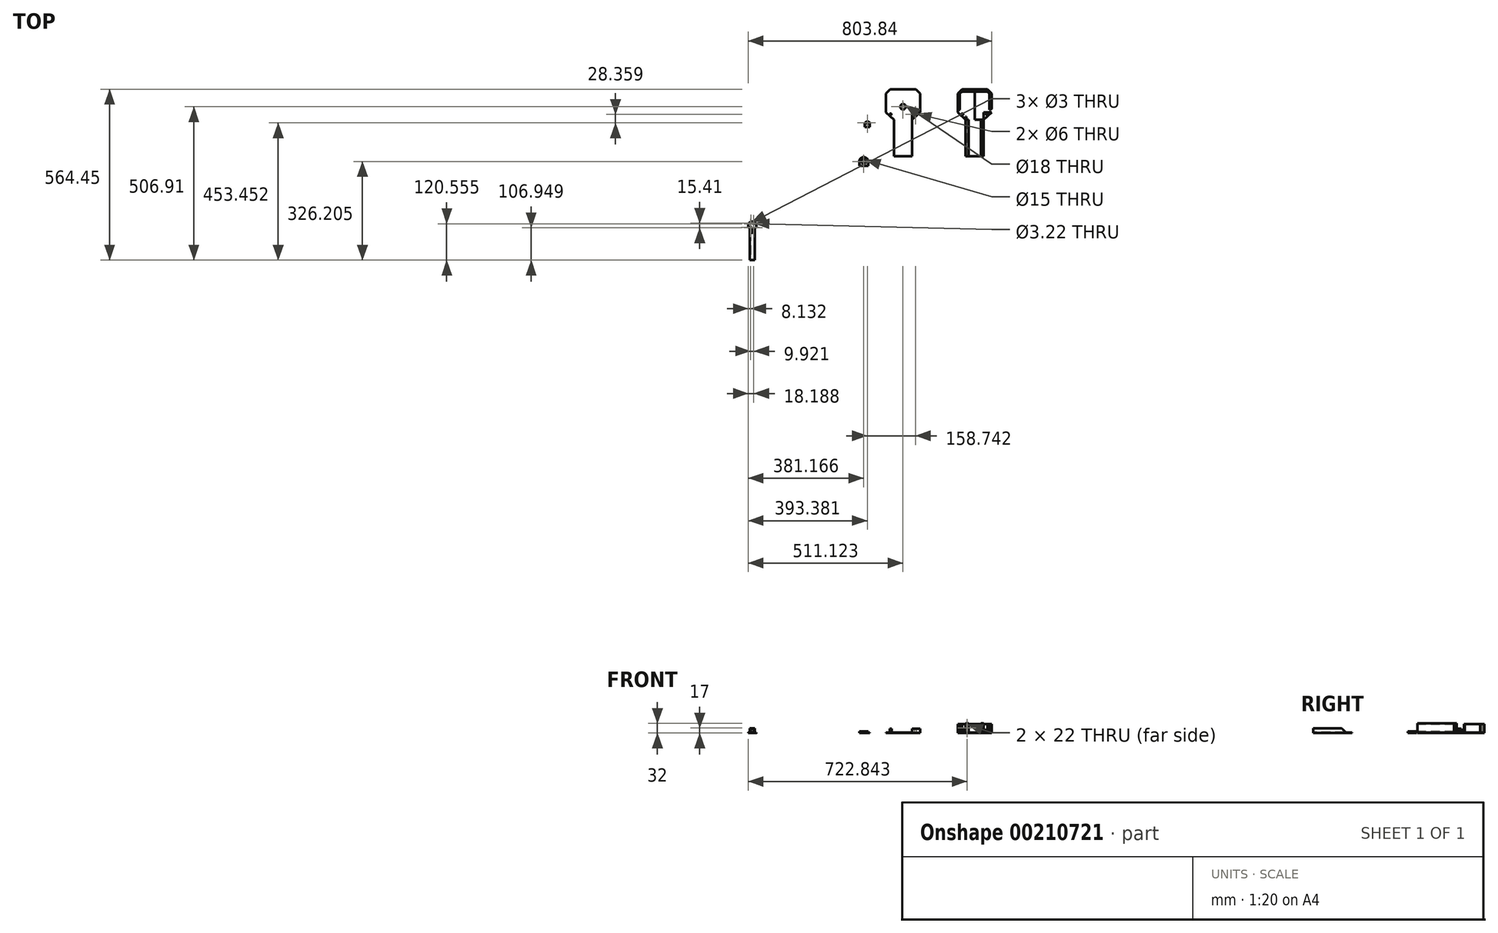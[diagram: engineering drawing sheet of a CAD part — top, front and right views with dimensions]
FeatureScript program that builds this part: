
annotation { "Feature Type Name" : "Feature", "Feature Type Description" : "" }
export const myFeature = defineFeature(function(context is Context, id is Id, definition is map)
    precondition{}
    {
        {
            var Q0;
            Q0=qCreatedBy(makeId("Top.planeOp"),FACE);
            var sketch = newSketch(context, id + "F0", { "sketchPlane" : qUnion([Q0])});
            skLineSegment(sketch, "E0.bottom", {"start": v(135.29, -55.36) * mm, "end": v(160.29, -55.36) * mm});
            skLineSegment(sketch, "E0.top", {"start": v(135.29, -70.36) * mm, "end": v(160.29, -70.36) * mm});
            skLineSegment(sketch, "E0.left", {"start": v(135.29, -55.36) * mm, "end": v(135.29, -70.36) * mm});
            skLineSegment(sketch, "E0.right", {"start": v(160.29, -55.36) * mm, "end": v(160.29, -70.36) * mm});
            skArc(sketch, "E1", {"start": v(160.29, -55.36) * mm, "mid": v(147.79, -42.86) * mm, "end": v(135.29, -55.36) * mm});
            skPoint(sketch, "E2", {"position": v(147.79, -62.86) * mm});
            skLineSegment(sketch, "E3.bottom", {"start": v(133.29, -55.36) * mm, "end": v(162.29, -55.36) * mm});
            skLineSegment(sketch, "E3.top", {"start": v(133.29, -70.36) * mm, "end": v(162.29, -70.36) * mm});
            skLineSegment(sketch, "E3.left", {"start": v(133.29, -55.36) * mm, "end": v(133.29, -70.36) * mm});
            skLineSegment(sketch, "E3.right", {"start": v(162.29, -55.36) * mm, "end": v(162.29, -70.36) * mm});
            skArc(sketch, "E4", {"start": v(162.29, -55.36) * mm, "mid": v(147.79, -40.86) * mm, "end": v(133.29, -55.36) * mm});
            skLineSegment(sketch, "E5", {"start": v(135.29, -68.36) * mm, "end": v(160.29, -68.36) * mm});
            skPoint(sketch, "E6", {"position": v(162.29, -63.36) * mm});
            skPoint(sketch, "E7", {"position": v(133.29, -63.36) * mm});
            skCircle(sketch, "E8", {"center": v(-219.9, -267.1) * mm, "radius": 13.48 * mm});
            skPoint(sketch, "E9", {"position": v(-225.25, -272.96) * mm});
            skPoint(sketch, "E10", {"position": v(-225.04, -259.21) * mm});
            skPoint(sketch, "E11", {"position": v(-215.33, -274.62) * mm});
            skPoint(sketch, "E12", {"position": v(-215.2, -261.01) * mm});
            skCircle(sketch, "E13", {"center": v(-225.04, -259.21) * mm, "radius": 1.5 * mm});
            skCircle(sketch, "E14", {"center": v(-215.2, -261.01) * mm, "radius": 1.61 * mm});
            skCircle(sketch, "E15", {"center": v(-215.33, -274.62) * mm, "radius": 1.5 * mm});
            skCircle(sketch, "E16", {"center": v(-225.25, -272.96) * mm, "radius": 1.5 * mm});
            skLineSegment(sketch, "E17", {"start": v(-215.33, -274.62) * mm, "end": v(-215.33, -273.12) * mm});
            skLineSegment(sketch, "E18", {"start": v(-215.33, -259.4) * mm, "end": v(-215.33, -262.62) * mm});
            skLineSegment(sketch, "E19", {"start": v(-225.04, -259.21) * mm, "end": v(-225.06, -260.71) * mm});
            skLineSegment(sketch, "E20", {"start": v(-225.25, -272.96) * mm, "end": v(-225.25, -274.46) * mm});
            skLineSegment(sketch, "E21", {"start": v(-225.25, -279.48) * mm, "end": v(-225.23, -277.57) * mm});
            skLineSegment(sketch, "E22", {"start": v(-225.04, -259.21) * mm, "end": v(-225.04, -254.64) * mm});
            skLineSegment(sketch, "E23.bottom", {"start": v(-225.25, -277.57) * mm, "end": v(-225.23, -277.57) * mm});
            skLineSegment(sketch, "E23.top", {"start": v(-228.4, -381.57) * mm, "end": v(-211.4, -381.57) * mm});
            skLineSegment(sketch, "E23.left", {"start": v(-228.4, -277.57) * mm, "end": v(-228.4, -381.57) * mm});
            skLineSegment(sketch, "E23.right", {"start": v(-211.4, -277.57) * mm, "end": v(-211.4, -381.57) * mm});
            skLineSegment(sketch, "E24.trimOffspring", {"start": v(-215.33, -273.12) * mm, "end": v(-215.33, -276.12) * mm});
            skPoint(sketch, "E25.orphan", {"position": v(-215.33, -279.78) * mm});
            skLineSegment(sketch, "E26.trimOffspring", {"start": v(-215.33, -262.62) * mm, "end": v(-215.33, -254.42) * mm});
            skLineSegment(sketch, "E27.trimOffspring", {"start": v(-225.23, -271.46) * mm, "end": v(-225.25, -272.96) * mm});
            skLineSegment(sketch, "E28.trimOffspring", {"start": v(-225.2, -274.45) * mm, "end": v(-225.16, -271.46) * mm});
            skLineSegment(sketch, "E29.trimOffspring", {"start": v(-225.05, -260.71) * mm, "end": v(-225.04, -259.21) * mm});
            skSolve(sketch);
        }
        {
            var Q0;
            {var subQ0=sQuery(id+"F0.wireOp",EDGE,"E1");Q0=makeQuery(id+"F0.imprint","IMPRINT",FACE,{"disambiguationData":[TD([[makeQuery(id+"F0.imprint","IMPRINT",EDGE,{"derivedFrom":subQ0}),-1.0]])]});}
            var Q1;
            {var subQ3=sQuery(id+"F0.wireOp",EDGE,"E3.right");Q1=makeQuery(id+"F0.imprint","IMPRINT",FACE,{"disambiguationData":[TD([[makeQuery(id+"F0.imprint","IMPRINT",EDGE,{"derivedFrom":subQ3}),-1.0]])]});}
            var Q2;
            {var subQ3=sQuery(id+"F0.wireOp",EDGE,"E5");Q2=makeQuery(id+"F0.imprint","IMPRINT",FACE,{"disambiguationData":[TD([[makeQuery(id+"F0.imprint","IMPRINT",EDGE,{"derivedFrom":subQ3}),-1.0]])]});}
            var Q3;
            {var subQ3=sQuery(id+"F0.wireOp",EDGE,"E3.left");Q3=makeQuery(id+"F0.imprint","IMPRINT",FACE,{"disambiguationData":[TD([[makeQuery(id+"F0.imprint","IMPRINT",EDGE,{"derivedFrom":subQ3}),1.0]])]});}
            var Q4;
            {var subQ4=sQuery(id+"F0.wireOp",EDGE,"E5");Q4=makeQuery(id+"F0.imprint","IMPRINT",FACE,{"disambiguationData":[TD([[makeQuery(id+"F0.imprint","IMPRINT",EDGE,{"derivedFrom":subQ4}),1.0]])]});}
            var Q5;
            {var subQ0=sQuery(id+"F0.wireOp",EDGE,"E1");Q5=makeQuery(id+"F0.imprint","IMPRINT",FACE,{"disambiguationData":[TD([[makeQuery(id+"F0.imprint","IMPRINT",EDGE,{"derivedFrom":subQ0}),1.0]])]});}
            extrude(context, id + "F1", {"entities" : qUnion([Q0, Q1, Q2, Q3, Q4, Q5]), "depth" : 5 * mm});
        }
        {
            var Q0;
            Q0=sQuery(id+"F0.wireOp",VERTEX,"E4.center");
            var Q1;
            Q1=makeQuery(id+"F1.opExtrude","SWEPT_BODY",BODY,{"disambiguationData":[OSD([sQuery(id+"F0.wireOp",EDGE,"E3.top"),sQuery(id+"F0.wireOp",EDGE,"E3.left"),sQuery(id+"F0.wireOp",EDGE,"E3.right"),sQuery(id+"F0.wireOp",EDGE,"E4")])]});
            hole(context, id + "F2", {"style" : HoleStyle.SIMPLE, "endStyle" : HoleEndStyle.BLIND, "oppositeDirection" : true, "holeDiameter" : 15 * mm, "holeDepth" : 12 * mm, "tappedDepth" : 12 * mm, "tapClearance" : 3, "locations" : qUnion([Q0]), "scope" : qUnion([Q1])});
        }
        {
            var Q0;
            Q0=qCreatedBy(makeId("Top.planeOp"),FACE);
            var sketch = newSketch(context, id + "F3", { "sketchPlane" : qUnion([Q0])});
            skLineSegment(sketch, "E30.bottom", {"start": v(247.74, 82.27) * mm, "end": v(307.74, 82.27) * mm});
            skLineSegment(sketch, "E30.top", {"start": v(247.74, -37.73) * mm, "end": v(307.74, -37.73) * mm});
            skLineSegment(sketch, "E30.left", {"start": v(247.74, 82.27) * mm, "end": v(247.74, -37.73) * mm});
            skLineSegment(sketch, "E30.right", {"start": v(307.74, 82.27) * mm, "end": v(307.74, -37.73) * mm});
            skPoint(sketch, "E31.MirrorCS.start.orphan", {"position": v(308.47, -37.03) * mm});
            skPoint(sketch, "E32.end.orphan", {"position": v(277.74, -37.73) * mm});
            skPoint(sketch, "E32.start.orphan", {"position": v(277.74, 82.27) * mm});
            skLineSegment(sketch, "E33", {"start": v(257.74, 82.27) * mm, "end": v(257.74, -37.73) * mm});
            skLineSegment(sketch, "E34", {"start": v(297.74, -37.73) * mm, "end": v(297.74, 82.27) * mm});
            skLineSegment(sketch, "E35.bottom", {"start": v(-60.02, 19.85) * mm, "end": v(-48.02, 19.85) * mm});
            skLineSegment(sketch, "E35.top", {"start": v(-60.02, 7.85) * mm, "end": v(-48.02, 7.85) * mm});
            skLineSegment(sketch, "E35.left", {"start": v(-60.02, 19.85) * mm, "end": v(-60.02, 7.85) * mm});
            skLineSegment(sketch, "E35.right", {"start": v(-48.02, 19.85) * mm, "end": v(-48.02, 7.85) * mm});
            skLineSegment(sketch, "E36", {"start": v(277.74, 182.88) * mm, "end": v(319.8, 182.88) * mm});
            skLineSegment(sketch, "E37", {"start": v(277.74, 182.88) * mm, "end": v(235.68, 182.88) * mm});
            skLineSegment(sketch, "E38", {"start": v(221.74, 168.95) * mm, "end": v(221.74, 107.24) * mm});
            skLineSegment(sketch, "E39", {"start": v(333.74, 168.95) * mm, "end": v(333.74, 107.24) * mm});
            skLineSegment(sketch, "E40", {"start": v(307.74, 82.27) * mm, "end": v(333.74, 107.24) * mm});
            skLineSegment(sketch, "E41.MirrorCS", {"start": v(247.74, 82.2) * mm, "end": v(221.74, 107.24) * mm});
            skLineSegment(sketch, "E42", {"start": v(277.74, 182.88) * mm, "end": v(277.74, -37.73) * mm});
            skLineSegment(sketch, "E43", {"start": v(247.74, 82.27) * mm, "end": v(247.74, 107.24) * mm});
            skLineSegment(sketch, "E44", {"start": v(247.74, 107.24) * mm, "end": v(221.74, 107.24) * mm});
            skCircle(sketch, "E45", {"center": v(236.74, 100.24) * mm, "radius": 3 * mm});
            skLineSegment(sketch, "E46", {"start": v(236.74, 103.24) * mm, "end": v(236.74, 97.24) * mm});
            skLineSegment(sketch, "E47.bottom", {"start": v(151.5, 68.38) * mm, "end": v(168.5, 68.38) * mm});
            skLineSegment(sketch, "E47.top", {"start": v(151.5, 58.38) * mm, "end": v(168.5, 58.38) * mm});
            skLineSegment(sketch, "E47.left", {"start": v(151.5, 68.38) * mm, "end": v(151.5, 58.38) * mm});
            skLineSegment(sketch, "E47.right", {"start": v(168.5, 68.38) * mm, "end": v(168.5, 58.38) * mm});
            skLineSegment(sketch, "E48", {"start": v(160, 68.38) * mm, "end": v(160, 76.88) * mm});
            skPoint(sketch, "E49", {"position": v(160, 74.88) * mm});
            skPoint(sketch, "E50", {"position": v(160, 68.88) * mm});
            skLineSegment(sketch, "E51", {"start": v(160, 74.88) * mm, "end": v(160, 68.88) * mm});
            skCircle(sketch, "E52", {"center": v(160, 71.88) * mm, "radius": 3 * mm});
            skArc(sketch, "E53", {"start": v(168.5, 68.38) * mm, "mid": v(160, 76.88) * mm, "end": v(151.5, 68.38) * mm});
            skCircle(sketch, "E54.MirrorC", {"center": v(318.74, 100.24) * mm, "radius": 3 * mm});
            skLineSegment(sketch, "E55.MirrorCS", {"start": v(307.74, 82.27) * mm, "end": v(307.74, 107.24) * mm});
            skLineSegment(sketch, "E56.MirrorCS", {"start": v(307.74, 107.24) * mm, "end": v(333.74, 107.24) * mm});
            skLineSegment(sketch, "E57", {"start": v(221.74, 168.95) * mm, "end": v(235.68, 182.88) * mm});
            skLineSegment(sketch, "E58.MirrorCS", {"start": v(333.74, 168.95) * mm, "end": v(319.8, 182.88) * mm});
            skPoint(sketch, "E59.endSnap0", {"position": v(228.7, 175.92) * mm});
            skLineSegment(sketch, "E60.MirrorCS", {"start": v(556.53, 182.88) * mm, "end": v(556.53, 175.92) * mm});
            skLineSegment(sketch, "E61.MirrorCS", {"start": v(570.46, 168.95) * mm, "end": v(556.53, 182.88) * mm});
            skLineSegment(sketch, "E62.MirrorCS", {"start": v(555.46, 103.24) * mm, "end": v(555.46, 97.24) * mm});
            skArc(sketch, "E63.MirrorCS", {"start": v(563.5, 118.67) * mm, "mid": v(563.39, 117.04) * mm, "end": v(563.06, 115.43) * mm});
            skLineSegment(sketch, "E64.MirrorCS", {"start": v(556.53, 175.92) * mm, "end": v(563.5, 168.95) * mm});
            skCircle(sketch, "E65.MirrorC", {"center": v(555.46, 100.24) * mm, "radius": 3 * mm});
            skCircle(sketch, "E66.MirrorC", {"center": v(473.46, 100.24) * mm, "radius": 3 * mm});
            skLineSegment(sketch, "E67.MirrorCS", {"start": v(458.46, 168.95) * mm, "end": v(472.4, 182.88) * mm});
            skLineSegment(sketch, "E68.MirrorCS", {"start": v(544.46, 82.27) * mm, "end": v(544.46, 107.24) * mm});
            skLineSegment(sketch, "E69.MirrorCS", {"start": v(556.53, 175.92) * mm, "end": v(514.46, 175.92) * mm});
            skLineSegment(sketch, "E70.MirrorCS", {"start": v(484.92, 107.24) * mm, "end": v(458.92, 107.24) * mm});
            skLineSegment(sketch, "E71.MirrorCS", {"start": v(514.46, 182.88) * mm, "end": v(514.46, -37.73) * mm});
            skLineSegment(sketch, "E72.MirrorCS", {"start": v(514.46, 182.88) * mm, "end": v(556.53, 182.88) * mm});
            skLineSegment(sketch, "E73.MirrorCS", {"start": v(563.5, 140.07) * mm, "end": v(563.5, 168.95) * mm});
            skLineSegment(sketch, "E74.MirrorCS", {"start": v(534.46, 82.27) * mm, "end": v(534.46, -37.73) * mm});
            skLineSegment(sketch, "E75.MirrorCS", {"start": v(494.46, -37.73) * mm, "end": v(494.46, 82.27) * mm});
            skLineSegment(sketch, "E76.MirrorCS", {"start": v(570.46, 168.95) * mm, "end": v(570.46, 107.24) * mm});
            skPoint(sketch, "E77.MirrorP", {"position": v(514.46, -37.73) * mm});
            skLineSegment(sketch, "E78.MirrorCS", {"start": v(544.46, 107.24) * mm, "end": v(570.46, 107.24) * mm});
            skPoint(sketch, "E79.MirrorP", {"position": v(514.46, 82.27) * mm});
            skLineSegment(sketch, "E80.MirrorCS", {"start": v(544.46, 82.2) * mm, "end": v(570.46, 107.24) * mm});
            skLineSegment(sketch, "E81.MirrorCS", {"start": v(484.46, 82.27) * mm, "end": v(458.46, 107.24) * mm});
            skLineSegment(sketch, "E82.MirrorCS", {"start": v(514.46, 182.88) * mm, "end": v(472.4, 182.88) * mm});
            skPoint(sketch, "E83.MirrorP", {"position": v(563.5, 175.92) * mm});
            skLineSegment(sketch, "E84.MirrorCS", {"start": v(458.46, 168.95) * mm, "end": v(458.46, 107.24) * mm});
            skPoint(sketch, "E85.MirrorP", {"position": v(483.74, -37.03) * mm});
            skLineSegment(sketch, "E86.MirrorCS", {"start": v(484.46, 82.27) * mm, "end": v(484.46, 107.24) * mm});
            skLineSegment(sketch, "E87.MirrorCS", {"start": v(563.5, 140.07) * mm, "end": v(563.5, 118.67) * mm});
            skLineSegment(sketch, "E88.MirrorCS", {"start": v(544.46, 82.27) * mm, "end": v(484.46, 82.27) * mm});
            skLineSegment(sketch, "E89.MirrorCS", {"start": v(544.46, 82.27) * mm, "end": v(544.46, -37.73) * mm});
            skLineSegment(sketch, "E90.MirrorCS", {"start": v(544.46, -37.73) * mm, "end": v(484.46, -37.73) * mm});
            skLineSegment(sketch, "E91.MirrorCS", {"start": v(484.46, 82.27) * mm, "end": v(484.46, -37.73) * mm});
            skLineSegment(sketch, "E92.MirrorCS", {"start": v(472.4, 175.92) * mm, "end": v(514.46, 175.92) * mm});
            skLineSegment(sketch, "E93.MirrorCS", {"start": v(472.4, 175.92) * mm, "end": v(465.43, 168.95) * mm});
            skLineSegment(sketch, "E94.MirrorCS", {"start": v(465.43, 140.07) * mm, "end": v(465.43, 168.95) * mm});
            skLineSegment(sketch, "E95.MirrorCS", {"start": v(465.43, 140.07) * mm, "end": v(465.43, 118.67) * mm});
            skArc(sketch, "E96.MirrorCS", {"start": v(465.43, 118.67) * mm, "mid": v(465.54, 117.04) * mm, "end": v(465.87, 115.43) * mm});
            skLineSegment(sketch, "E97.MirrorCS", {"start": v(559.97, 107.24) * mm, "end": v(559.97, 107.24) * mm});
            skLineSegment(sketch, "E98.MirrorCS", {"start": v(325.78, 167.98) * mm, "end": v(325.78, 168.95) * mm});
            skLineSegment(sketch, "E99", {"start": v(458.92, 107.24) * mm, "end": v(458.46, 107.24) * mm});
            skPoint(sketch, "E100.MirrorCS.end.orphan", {"position": v(322.24, 107.24) * mm});
            skPoint(sketch, "E100.MirrorCS.start.orphan", {"position": v(322.24, 110.06) * mm});
            skPoint(sketch, "E101.MirrorCS.start.orphan", {"position": v(325.78, 118.67) * mm});
            skPoint(sketch, "E102.MirrorCS.end.orphan", {"position": v(326.75, 118.67) * mm});
            skPoint(sketch, "E102.MirrorCS.start.orphan", {"position": v(326.75, 140.07) * mm});
            skPoint(sketch, "E103.MirrorCS.end.orphan", {"position": v(325.78, 167.98) * mm});
            skPoint(sketch, "E104.MirrorCS.end.orphan", {"position": v(323.2, 110.06) * mm});
            skPoint(sketch, "E105.MirrorCS.end.orphan", {"position": v(323.2, 107.24) * mm});
            skPoint(sketch, "E106.MirrorCS.end.orphan", {"position": v(326.78, 168.95) * mm});
            skPoint(sketch, "E107.MirrorCS.start.orphan", {"position": v(319.8, 175.92) * mm});
            skPoint(sketch, "E108.MirrorCS.end.orphan", {"position": v(319.8, 174.92) * mm});
            skPoint(sketch, "E108.MirrorCS.start.orphan", {"position": v(325.78, 168.95) * mm});
            skPoint(sketch, "E109.MirrorCS.end.orphan", {"position": v(277.74, 174.92) * mm});
            skPoint(sketch, "E110.MirrorCS.end.orphan", {"position": v(277.74, 175.92) * mm});
            skPoint(sketch, "E111.end.orphan", {"position": v(228.7, 168.95) * mm});
            skPoint(sketch, "E112.end.orphan", {"position": v(229.7, 168.95) * mm});
            skPoint(sketch, "E112.start.orphan", {"position": v(229.7, 167.98) * mm});
            skPoint(sketch, "E113.end.orphan", {"position": v(235.68, 174.92) * mm});
            skPoint(sketch, "E113.start.orphan", {"position": v(235.68, 175.92) * mm});
            skPoint(sketch, "E114.start.orphan", {"position": v(228.74, 140.07) * mm});
            skPoint(sketch, "E115.end.orphan", {"position": v(229.7, 118.67) * mm});
            skPoint(sketch, "E115.start.orphan", {"position": v(228.74, 118.67) * mm});
            skPoint(sketch, "E116.end.orphan", {"position": v(232.28, 107.24) * mm});
            skPoint(sketch, "E116.start.orphan", {"position": v(232.28, 110.06) * mm});
            skPoint(sketch, "E117.end.orphan", {"position": v(233.25, 107.24) * mm});
            skPoint(sketch, "E117.start.orphan", {"position": v(233.25, 110.06) * mm});
            skLineSegment(sketch, "E118", {"start": v(319.8, 182.88) * mm, "end": v(379.35, 182.88) * mm});
            skLineSegment(sketch, "E119", {"start": v(379.35, 182.88) * mm, "end": v(379.35, -37.03) * mm});
            skCircle(sketch, "E120", {"center": v(277.74, 125.34) * mm, "radius": 9 * mm});
            skLineSegment(sketch, "E121", {"start": v(277.74, 125.34) * mm, "end": v(286.74, 125.34) * mm});
            skLineSegment(sketch, "E122", {"start": v(566.51, 115.43) * mm, "end": v(570.46, 118.67) * mm});
            skPoint(sketch, "E123.orphan", {"position": v(559.97, 110.06) * mm});
            skLineSegment(sketch, "E124.MirrorCS", {"start": v(462.41, 115.43) * mm, "end": v(458.46, 118.67) * mm});
            skPoint(sketch, "E125.end.orphan", {"position": v(468.96, 107.24) * mm});
            skLineSegment(sketch, "E126", {"start": v(462.41, 115.43) * mm, "end": v(465.87, 115.43) * mm});
            skPoint(sketch, "E127.orphan", {"position": v(468.96, 110.06) * mm});
            skPoint(sketch, "E128", {"position": v(486.46, 82.27) * mm});
            skLineSegment(sketch, "E129", {"start": v(486.46, 82.27) * mm, "end": v(486.46, 92.16) * mm});
            skLineSegment(sketch, "E130", {"start": v(486.46, 92.16) * mm, "end": v(484.46, 92.16) * mm});
            skLineSegment(sketch, "E131.MirrorCS", {"start": v(566.51, 115.43) * mm, "end": v(563.06, 115.43) * mm});
            skSolve(sketch);
        }
        {
            var Q0;
            Q0=makeQuery(id+"F3.imprint","IMPRINT",FACE,{"disambiguationData":[TD([[makeQuery(id+"F3.imprint","IMPRINT",EDGE,{"derivedFrom":sQuery(id+"F3.wireOp",EDGE,"E47.top")}),1.0]])]});
            var Q1;
            {var subQ1=sQuery(id+"F3.wireOp",EDGE,"E48");var subQ7=sQuery(id+"F3.wireOp",EDGE,"E47.bottom");var subQ8=makeQuery(id+"F3.imprint","INTERSECT",VERTEX,{"derivedFrom":[subQ7,subQ1]});Q1=makeQuery(id+"F3.imprint","IMPRINT",FACE,{"disambiguationData":[TD([[makeQuery(id+"F3.imprint","IMPRINT",EDGE,{"disambiguationData":[TD([[subQ8,-1.0]])],"derivedFrom":subQ7}),1.0]])]});}
            var Q2;
            {var subQ0=sQuery(id+"F3.wireOp",EDGE,"E48");var subQ1=sQuery(id+"F3.wireOp",EDGE,"E47.bottom");var subQ2=makeQuery(id+"F3.imprint","INTERSECT",VERTEX,{"derivedFrom":[subQ1,subQ0]});Q2=makeQuery(id+"F3.imprint","IMPRINT",FACE,{"disambiguationData":[TD([[makeQuery(id+"F3.imprint","IMPRINT",EDGE,{"disambiguationData":[TD([[subQ2,1.0]])],"derivedFrom":subQ1}),1.0]])]});}
            extrude(context, id + "F4", {"entities" : qUnion([Q0, Q1, Q2]), "depth" : 2 * mm});
        }
        {
            var Q0;
            Q0=makeQuery(id+"F0.imprint","IMPRINT",FACE,{"disambiguationData":[TD([[makeQuery(id+"F0.imprint","IMPRINT",EDGE,{"derivedFrom":sQuery(id+"F0.wireOp",EDGE,"E23.top")}),1.0]])]});
            extrude(context, id + "F5", {"entities" : qUnion([Q0]), "depth" : 16 * mm});
        }
        {
            var Q0;
            {var subQ11=sQuery(id+"F0.wireOp",EDGE,"E8");var subQ12=makeQuery(id+"F0.imprint","IMPRINT",VERTEX,{"disambiguationData":[OD(1.0)],"derivedFrom":subQ11});Q0=makeQuery(id+"F0.imprint","IMPRINT",FACE,{"disambiguationData":[TD([[makeQuery(id+"F0.imprint","IMPRINT",EDGE,{"disambiguationData":[TD([[subQ12,1.0]])],"derivedFrom":subQ11}),1.0]])]});}
            extrude(context, id + "F6", {"entities" : qUnion([Q0]), "operationType" : NewBodyOperationType.ADD, "depth" : 2 * mm});
        }
        {
            var Q0;
            Q0=makeQuery(id+"F3.imprint","IMPRINT",FACE,{"disambiguationData":[TD([[makeQuery(id+"F3.imprint","IMPRINT",EDGE,{"derivedFrom":sQuery(id+"F3.wireOp",EDGE,"E67.MirrorCS")}),-1.0]])]});
            var Q1;
            Q1=makeQuery(id+"F3.imprint","IMPRINT",FACE,{"disambiguationData":[TD([[makeQuery(id+"F3.imprint","IMPRINT",EDGE,{"derivedFrom":sQuery(id+"F3.wireOp",EDGE,"E60.MirrorCS")}),-1.0]])]});
            var Q2;
            Q2=makeQuery(id+"F3.imprint","IMPRINT",FACE,{"disambiguationData":[TD([[makeQuery(id+"F3.imprint","IMPRINT",EDGE,{"derivedFrom":sQuery(id+"F3.wireOp",EDGE,"E60.MirrorCS")}),1.0]])]});
            var Q3;
            {var subQ0=sQuery(id+"F3.wireOp",EDGE,"E75.MirrorCS");Q3=makeQuery(id+"F3.imprint","IMPRINT",FACE,{"disambiguationData":[TD([[makeQuery(id+"F3.imprint","IMPRINT",EDGE,{"derivedFrom":subQ0}),1.0]])]});}
            var Q4;
            {var subQ4=sQuery(id+"F3.wireOp",EDGE,"E74.MirrorCS");Q4=makeQuery(id+"F3.imprint","IMPRINT",FACE,{"disambiguationData":[TD([[makeQuery(id+"F3.imprint","IMPRINT",EDGE,{"derivedFrom":subQ4}),1.0]])]});}
            var Q5;
            {var subQ4=sQuery(id+"F3.wireOp",EDGE,"E129");Q5=makeQuery(id+"F3.imprint","IMPRINT",FACE,{"disambiguationData":[TD([[makeQuery(id+"F3.imprint","IMPRINT",EDGE,{"derivedFrom":subQ4}),1.0]])]});}
            extrude(context, id + "F7", {"entities" : qUnion([Q0, Q1, Q2, Q3, Q4, Q5]), "depth" : 30 * mm});
        }
        {
            var Q0;
            {var subQ5=sQuery(id+"F3.wireOp",EDGE,"E86.MirrorCS");Q0=makeQuery(id+"F3.imprint","IMPRINT",FACE,{"disambiguationData":[TD([[makeQuery(id+"F3.imprint","IMPRINT",EDGE,{"derivedFrom":subQ5}),-1.0]])]});}
            var Q1;
            Q1=makeQuery(id+"F3.imprint","IMPRINT",FACE,{"disambiguationData":[TD([[makeQuery(id+"F3.imprint","IMPRINT",EDGE,{"derivedFrom":sQuery(id+"F3.wireOp",EDGE,"E63.MirrorCS")}),-1.0]])]});
            var Q2;
            {var subQ5=sQuery(id+"F3.wireOp",EDGE,"E74.MirrorCS");Q2=makeQuery(id+"F3.imprint","IMPRINT",FACE,{"disambiguationData":[TD([[makeQuery(id+"F3.imprint","IMPRINT",EDGE,{"derivedFrom":subQ5}),-1.0]])]});}
            var Q3;
            {var subQ5=sQuery(id+"F3.wireOp",EDGE,"E75.MirrorCS");Q3=makeQuery(id+"F3.imprint","IMPRINT",FACE,{"disambiguationData":[TD([[makeQuery(id+"F3.imprint","IMPRINT",EDGE,{"derivedFrom":subQ5}),-1.0]])]});}
            var Q4;
            Q4=makeQuery(id+"F3.imprint","IMPRINT",FACE,{"disambiguationData":[TD([[makeQuery(id+"F3.imprint","IMPRINT",EDGE,{"derivedFrom":sQuery(id+"F3.wireOp",EDGE,"E66.MirrorC")}),-1.0]])]});
            var Q5;
            {var subQ1=sQuery(id+"F3.wireOp",EDGE,"E68.MirrorCS");Q5=makeQuery(id+"F3.imprint","IMPRINT",FACE,{"disambiguationData":[TD([[makeQuery(id+"F3.imprint","IMPRINT",EDGE,{"derivedFrom":subQ1}),-1.0]])]});}
            var Q6;
            Q6=makeQuery(id+"F3.imprint","IMPRINT",FACE,{"disambiguationData":[TD([[makeQuery(id+"F3.imprint","IMPRINT",EDGE,{"derivedFrom":sQuery(id+"F3.wireOp",EDGE,"E67.MirrorCS")}),-1.0]])]});
            var Q7;
            Q7=makeQuery(id+"F3.imprint","IMPRINT",FACE,{"disambiguationData":[TD([[makeQuery(id+"F3.imprint","IMPRINT",EDGE,{"derivedFrom":sQuery(id+"F3.wireOp",EDGE,"E60.MirrorCS")}),1.0]])]});
            var Q8;
            Q8=makeQuery(id+"F3.imprint","IMPRINT",FACE,{"disambiguationData":[TD([[makeQuery(id+"F3.imprint","IMPRINT",EDGE,{"derivedFrom":sQuery(id+"F3.wireOp",EDGE,"E60.MirrorCS")}),-1.0]])]});
            var Q9;
            {var subQ4=sQuery(id+"F3.wireOp",EDGE,"E74.MirrorCS");Q9=makeQuery(id+"F3.imprint","IMPRINT",FACE,{"disambiguationData":[TD([[makeQuery(id+"F3.imprint","IMPRINT",EDGE,{"derivedFrom":subQ4}),1.0]])]});}
            var Q10;
            {var subQ0=sQuery(id+"F3.wireOp",EDGE,"E75.MirrorCS");Q10=makeQuery(id+"F3.imprint","IMPRINT",FACE,{"disambiguationData":[TD([[makeQuery(id+"F3.imprint","IMPRINT",EDGE,{"derivedFrom":subQ0}),1.0]])]});}
            var Q11;
            {var subQ3=sQuery(id+"F3.wireOp",EDGE,"E92.MirrorCS");Q11=makeQuery(id+"F3.imprint","IMPRINT",FACE,{"disambiguationData":[TD([[makeQuery(id+"F3.imprint","IMPRINT",EDGE,{"derivedFrom":subQ3}),-1.0]])]});}
            extrude(context, id + "F8", {"entities" : qUnion([Q0, Q1, Q2, Q3, Q4, Q5, Q6, Q7, Q8, Q9, Q10, Q11]), "depth" : 2 * mm});
        }
        {
            var Q0;
            Q0=makeQuery(id+"F3.imprint","IMPRINT",FACE,{"disambiguationData":[TD([[makeQuery(id+"F3.imprint","IMPRINT",EDGE,{"derivedFrom":sQuery(id+"F3.wireOp",EDGE,"E66.MirrorC")}),1.0]])]});
            var Q1;
            {var subQ0=sQuery(id+"F3.wireOp",EDGE,"E62.MirrorCS");Q1=makeQuery(id+"F3.imprint","IMPRINT",FACE,{"disambiguationData":[TD([[makeQuery(id+"F3.imprint","IMPRINT",EDGE,{"derivedFrom":subQ0}),1.0]])]});}
            var Q2;
            {var subQ0=sQuery(id+"F3.wireOp",EDGE,"E62.MirrorCS");Q2=makeQuery(id+"F3.imprint","IMPRINT",FACE,{"disambiguationData":[TD([[makeQuery(id+"F3.imprint","IMPRINT",EDGE,{"derivedFrom":subQ0}),-1.0]])]});}
            extrude(context, id + "F9", {"entities" : qUnion([Q0, Q1, Q2]), "operationType" : NewBodyOperationType.ADD, "depth" : 15 * mm});
        }
        {
            var Q0;
            Q0=makeQuery(id+"F7.opExtrude","SWEPT_BODY",BODY,{"disambiguationData":[OSD([sQuery(id+"F3.wireOp",EDGE,"E74.MirrorCS"),sQuery(id+"F3.wireOp",EDGE,"E88.MirrorCS"),sQuery(id+"F3.wireOp",EDGE,"E89.MirrorCS"),sQuery(id+"F3.wireOp",EDGE,"E90.MirrorCS")])]});
            var Q1;
            Q1=makeQuery(id+"F7.opExtrude","SWEPT_BODY",BODY,{"disambiguationData":[OSD([sQuery(id+"F3.wireOp",EDGE,"E75.MirrorCS"),sQuery(id+"F3.wireOp",EDGE,"E88.MirrorCS"),sQuery(id+"F3.wireOp",EDGE,"E90.MirrorCS"),sQuery(id+"F3.wireOp",EDGE,"E91.MirrorCS")])]});
            transform(context, id + "F10", {"entities" : qUnion([Q0, Q1]), "transformType" : TransformType.TRANSLATION_3D, "dx" : 0 * mm, "dy" : 0 * mm, "dz" : 2 * mm, "makeCopy" : false});
        }
        {
            var Q0;
            {var subQ0=sQuery(id+"F3.wireOp",EDGE,"E90.MirrorCS");Q0=makeQuery(id+"F7.opExtrude","SWEPT_FACE",FACE,{"disambiguationData":[OSD([subQ0]),TDD([makeQuery(id+"F3.imprint","IMPRINT",EDGE,{"disambiguationData":[TD([[makeQuery(id+"F3.imprint","INTERSECT",VERTEX,{"derivedFrom":[sQuery(id+"F3.wireOp",EDGE,"E75.MirrorCS"),subQ0]}),-1.0]])],"derivedFrom":subQ0})])]});}
            var Q1;
            {var subQ0=sQuery(id+"F3.wireOp",EDGE,"E88.MirrorCS");Q1=makeQuery(id+"F7.opExtrude","SWEPT_FACE",FACE,{"disambiguationData":[OSD([subQ0]),TDD([makeQuery(id+"F3.imprint","IMPRINT",EDGE,{"disambiguationData":[TD([[makeQuery(id+"F3.imprint","INTERSECT",VERTEX,{"derivedFrom":[sQuery(id+"F3.wireOp",EDGE,"E75.MirrorCS"),subQ0]}),-1.0]])],"derivedFrom":subQ0})])]});}
            shell(context, id + "F11", {"entities" : qUnion([Q0, Q1]), "thickness" : 4 * mm});
        }
        {
            var Q0;
            {var subQ4=sQuery(id+"F3.wireOp",EDGE,"E37");Q0=makeQuery(id+"F3.imprint","IMPRINT",FACE,{"disambiguationData":[TD([[makeQuery(id+"F3.imprint","IMPRINT",EDGE,{"derivedFrom":subQ4}),1.0]])]});}
            var Q1;
            {var subQ0=sQuery(id+"F3.wireOp",EDGE,"E36");Q1=makeQuery(id+"F3.imprint","IMPRINT",FACE,{"disambiguationData":[TD([[makeQuery(id+"F3.imprint","IMPRINT",EDGE,{"derivedFrom":subQ0}),-1.0]])]});}
            var Q2;
            Q2=makeQuery(id+"F3.imprint","IMPRINT",FACE,{"disambiguationData":[TD([[makeQuery(id+"F3.imprint","IMPRINT",EDGE,{"derivedFrom":sQuery(id+"F3.wireOp",EDGE,"E40")}),1.0]])]});
            var Q3;
            {var subQ0=sQuery(id+"F3.wireOp",EDGE,"E30.right");Q3=makeQuery(id+"F3.imprint","IMPRINT",FACE,{"disambiguationData":[TD([[makeQuery(id+"F3.imprint","IMPRINT",EDGE,{"derivedFrom":subQ0}),-1.0]])]});}
            var Q4;
            {var subQ0=sQuery(id+"F3.wireOp",EDGE,"E34");Q4=makeQuery(id+"F3.imprint","IMPRINT",FACE,{"disambiguationData":[TD([[makeQuery(id+"F3.imprint","IMPRINT",EDGE,{"derivedFrom":subQ0}),1.0]])]});}
            var Q5;
            {var subQ0=sQuery(id+"F3.wireOp",EDGE,"E33");Q5=makeQuery(id+"F3.imprint","IMPRINT",FACE,{"disambiguationData":[TD([[makeQuery(id+"F3.imprint","IMPRINT",EDGE,{"derivedFrom":subQ0}),1.0]])]});}
            var Q6;
            {var subQ6=sQuery(id+"F3.wireOp",EDGE,"E33");Q6=makeQuery(id+"F3.imprint","IMPRINT",FACE,{"disambiguationData":[TD([[makeQuery(id+"F3.imprint","IMPRINT",EDGE,{"derivedFrom":subQ6}),-1.0]])]});}
            var Q7;
            {var subQ1=sQuery(id+"F3.wireOp",EDGE,"E41.MirrorCS");Q7=makeQuery(id+"F3.imprint","IMPRINT",FACE,{"disambiguationData":[TD([[makeQuery(id+"F3.imprint","IMPRINT",EDGE,{"derivedFrom":subQ1}),-1.0]])]});}
            extrude(context, id + "F12", {"entities" : qUnion([Q0, Q1, Q2, Q3, Q4, Q5, Q6, Q7]), "depth" : 2 * mm});
        }
        {
            var Q0;
            Q0=makeQuery(id+"F3.imprint","IMPRINT",FACE,{"disambiguationData":[TD([[makeQuery(id+"F3.imprint","IMPRINT",EDGE,{"derivedFrom":sQuery(id+"F3.wireOp",EDGE,"E54.MirrorC")}),-1.0]])]});
            var Q1;
            {var subQ0=sQuery(id+"F3.wireOp",EDGE,"E46");Q1=makeQuery(id+"F3.imprint","IMPRINT",FACE,{"disambiguationData":[TD([[makeQuery(id+"F3.imprint","IMPRINT",EDGE,{"derivedFrom":subQ0}),-1.0]])]});}
            var Q2;
            {var subQ0=sQuery(id+"F3.wireOp",EDGE,"E46");Q2=makeQuery(id+"F3.imprint","IMPRINT",FACE,{"disambiguationData":[TD([[makeQuery(id+"F3.imprint","IMPRINT",EDGE,{"derivedFrom":subQ0}),1.0]])]});}
            extrude(context, id + "F13", {"entities" : qUnion([Q0, Q1, Q2]), "operationType" : NewBodyOperationType.ADD, "depth" : 15 * mm});
        }
        {
            var Q0;
            Q0=makeQuery(id+"F5.opExtrude","CAP_EDGE",EDGE,{"disambiguationData":[OSD([sQuery(id+"F0.wireOp",EDGE,"E8")])],"isStart":false});
            chamfer(context, id + "F14", {"entities" : qUnion([Q0]), "width" : 10 * mm, "tangentPropagation" : true});
        }
        {
            var Q0;
            Q0=makeQuery(id+"F5.opExtrude","SWEPT_FACE",FACE,{"disambiguationData":[OSD([sQuery(id+"F0.wireOp",EDGE,"E8")])]});
            var Q1;
            Q1=makeQuery(id+"F14.opChamfer","BLEND_FACE",FACE,{"disambiguationData":[OSD([sQuery(id+"F0.wireOp",EDGE,"E8")])]});
            var Q2;
            Q2=makeQuery(id+"F5.opExtrude","SWEPT_FACE",FACE,{"disambiguationData":[OSD([sQuery(id+"F0.wireOp",EDGE,"E23.top")])]});
            shell(context, id + "F15", {"entities" : qUnion([Q0, Q1, Q2]), "thickness" : 2.5 * mm});
        }
    });
